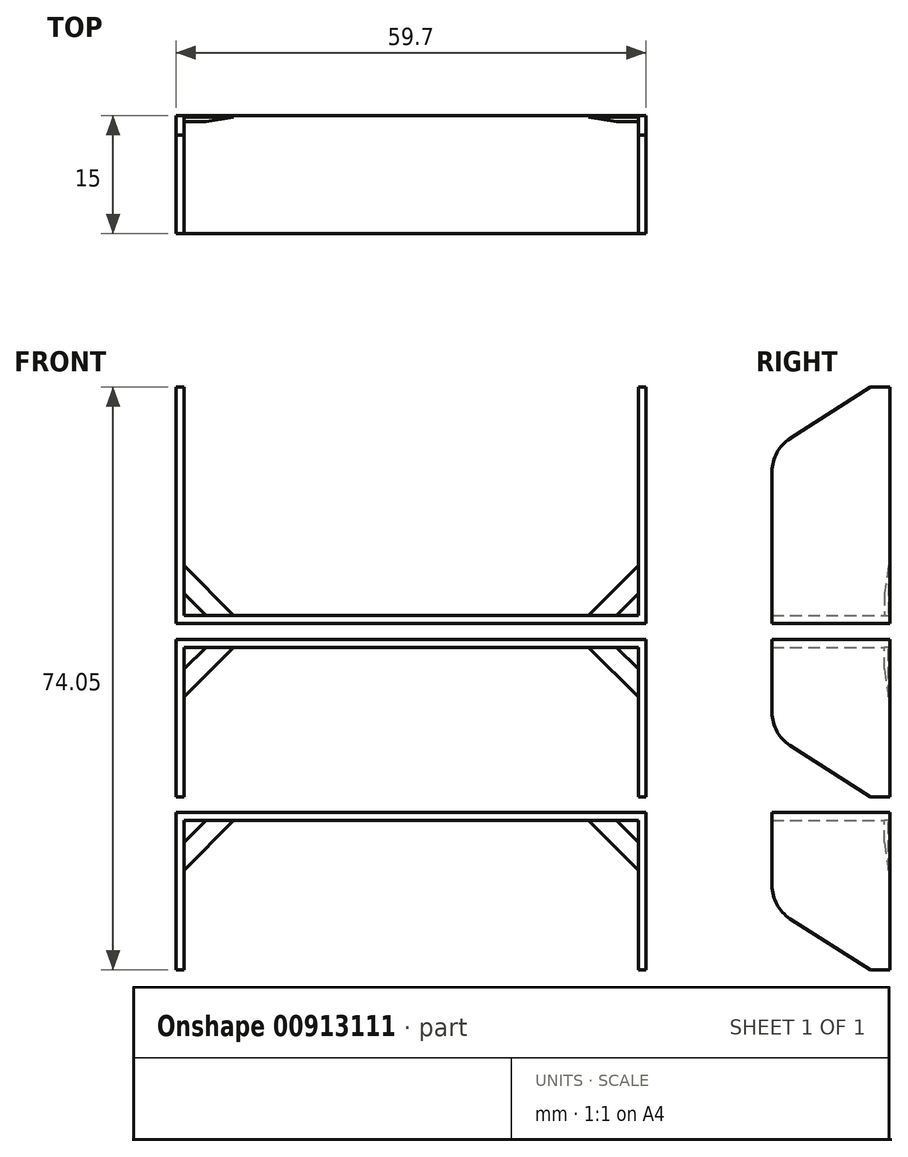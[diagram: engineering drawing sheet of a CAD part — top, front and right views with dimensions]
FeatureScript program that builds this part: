
annotation { "Feature Type Name" : "Feature", "Feature Type Description" : "" }
export const myFeature = defineFeature(function(context is Context, id is Id, definition is map)
    precondition{}
    {
        {
            var Q0;
            Q0=qCreatedBy(makeId("Front.planeOp"),FACE);
            var sketch = newSketch(context, id + "F0", { "sketchPlane" : qUnion([Q0])});
            skLineSegment(sketch, "E0", {"start": v(-40.12, 50.5) * mm, "end": v(-40.12, 20.5) * mm});
            skLineSegment(sketch, "E1", {"start": v(-40.12, 20.5) * mm, "end": v(19.58, 20.5) * mm});
            skLineSegment(sketch, "E2", {"start": v(19.58, 20.5) * mm, "end": v(19.58, 50.5) * mm});
            skLineSegment(sketch, "E3", {"start": v(-40.12, 50.5) * mm, "end": v(-39.12, 50.5) * mm});
            skLineSegment(sketch, "E4", {"start": v(-39.12, 50.5) * mm, "end": v(-39.12, 21.5) * mm});
            skLineSegment(sketch, "E5", {"start": v(-39.12, 21.5) * mm, "end": v(18.58, 21.5) * mm});
            skLineSegment(sketch, "E6", {"start": v(18.58, 21.5) * mm, "end": v(18.58, 50.5) * mm});
            skLineSegment(sketch, "E7", {"start": v(18.58, 50.5) * mm, "end": v(19.58, 50.5) * mm});
            skLineSegment(sketch, "E8", {"start": v(-39.12, 21.5) * mm, "end": v(-39.12, 20.5) * mm, "construction": true});
            skLineSegment(sketch, "E9", {"start": v(-39.12, 27.82) * mm, "end": v(-32.8, 21.5) * mm});
            skLineSegment(sketch, "E10", {"start": v(-10.27, 21.5) * mm, "end": v(-10.27, 32.03) * mm, "construction": true});
            skLineSegment(sketch, "E11.MirrorCS", {"start": v(18.58, 27.82) * mm, "end": v(12.27, 21.5) * mm});
            skSolve(sketch);
        }
        {
            var Q0;
            Q0=qCreatedBy(makeId("Front.planeOp"),FACE);
            var sketch = newSketch(context, id + "F1", { "sketchPlane" : qUnion([Q0])});
            skLineSegment(sketch, "E12", {"start": v(19.58, -1.54) * mm, "end": v(19.58, 18.46) * mm});
            skLineSegment(sketch, "E13", {"start": v(19.58, 18.46) * mm, "end": v(-40.12, 18.46) * mm});
            skLineSegment(sketch, "E14", {"start": v(-40.12, 18.46) * mm, "end": v(-40.12, -1.54) * mm});
            skLineSegment(sketch, "E15", {"start": v(19.58, -1.54) * mm, "end": v(18.58, -1.54) * mm});
            skLineSegment(sketch, "E16", {"start": v(18.58, -1.54) * mm, "end": v(18.58, 17.46) * mm});
            skLineSegment(sketch, "E17", {"start": v(18.58, 17.46) * mm, "end": v(-39.12, 17.46) * mm});
            skLineSegment(sketch, "E18", {"start": v(-39.12, 17.46) * mm, "end": v(-39.12, -1.54) * mm});
            skLineSegment(sketch, "E19", {"start": v(-39.12, -1.54) * mm, "end": v(-40.12, -1.54) * mm});
            skLineSegment(sketch, "E20", {"start": v(18.58, 17.46) * mm, "end": v(18.58, 18.46) * mm, "construction": true});
            skLineSegment(sketch, "E21", {"start": v(19.58, 20.5) * mm, "end": v(19.58, 10.1) * mm, "construction": true});
            skLineSegment(sketch, "E22", {"start": v(-32.8, 17.46) * mm, "end": v(-39.12, 11.14) * mm});
            skLineSegment(sketch, "E23", {"start": v(-10.27, 17.46) * mm, "end": v(-10.27, 10.79) * mm, "construction": true});
            skLineSegment(sketch, "E24.MirrorCS", {"start": v(12.27, 17.46) * mm, "end": v(18.58, 11.14) * mm});
            skSolve(sketch);
        }
        {
            var Q0;
            Q0=makeQuery(id+"F0.imprint","IMPRINT",FACE,{"disambiguationData":[TD([[makeQuery(id+"F0.imprint","IMPRINT",EDGE,{"derivedFrom":sQuery(id+"F0.wireOp",EDGE,"E0")}),1.0]])]});
            var Q1;
            Q1=makeQuery(id+"F1.imprint","IMPRINT",FACE,{"disambiguationData":[TD([[makeQuery(id+"F1.imprint","IMPRINT",EDGE,{"derivedFrom":sQuery(id+"F1.wireOp",EDGE,"E12")}),1.0]])]});
            extrude(context, id + "F2", {"entities" : qUnion([Q0, Q1]), "depth" : 15 * mm, "offsetDistance" : 25 * mm});
        }
        {
            var Q0;
            {var subQ3=sQuery(id+"F0.wireOp",EDGE,"E9");Q0=makeQuery(id+"F0.imprint","IMPRINT",FACE,{"disambiguationData":[TD([[makeQuery(id+"F0.imprint","IMPRINT",EDGE,{"derivedFrom":subQ3}),-1.0]])]});}
            var Q1;
            {var subQ3=sQuery(id+"F0.wireOp",EDGE,"E11.MirrorCS");Q1=makeQuery(id+"F0.imprint","IMPRINT",FACE,{"disambiguationData":[TD([[makeQuery(id+"F0.imprint","IMPRINT",EDGE,{"derivedFrom":subQ3}),1.0]])]});}
            var Q2;
            {var subQ3=sQuery(id+"F1.wireOp",EDGE,"E24.MirrorCS");Q2=makeQuery(id+"F1.imprint","IMPRINT",FACE,{"disambiguationData":[TD([[makeQuery(id+"F1.imprint","IMPRINT",EDGE,{"derivedFrom":subQ3}),1.0]])]});}
            var Q3;
            {var subQ3=sQuery(id+"F1.wireOp",EDGE,"E22");Q3=makeQuery(id+"F1.imprint","IMPRINT",FACE,{"disambiguationData":[TD([[makeQuery(id+"F1.imprint","IMPRINT",EDGE,{"derivedFrom":subQ3}),-1.0]])]});}
            extrude(context, id + "F3", {"entities" : qUnion([Q0, Q1, Q2, Q3]), "operationType" : NewBodyOperationType.ADD, "depth" : 0.75 * mm, "offsetDistance" : 25 * mm});
        }
        {
            var Q0;
            Q0=makeQuery(id+"F3.opExtrude","CAP_EDGE",EDGE,{"disambiguationData":[OSD([sQuery(id+"F0.wireOp",EDGE,"E11.MirrorCS")])],"isStart":false});
            var Q1;
            Q1=makeQuery(id+"F3.opExtrude","CAP_EDGE",EDGE,{"disambiguationData":[OSD([sQuery(id+"F1.wireOp",EDGE,"E24.MirrorCS")])],"isStart":false});
            chamfer(context, id + "F4", {"entities" : qUnion([Q0, Q1]), "chamferType" : ChamferType.TWO_OFFSETS, "width1" : 2.5 * mm, "oppositeDirection" : false, "width2" : 0.55 * mm, "tangentPropagation" : true});
        }
        {
            var Q0;
            Q0=makeQuery(id+"F3.opExtrude","CAP_EDGE",EDGE,{"disambiguationData":[OSD([sQuery(id+"F0.wireOp",EDGE,"E9")])],"isStart":false});
            var Q1;
            Q1=makeQuery(id+"F3.opExtrude","CAP_EDGE",EDGE,{"disambiguationData":[OSD([sQuery(id+"F1.wireOp",EDGE,"E22")])],"isStart":false});
            chamfer(context, id + "F5", {"entities" : qUnion([Q0, Q1]), "chamferType" : ChamferType.TWO_OFFSETS, "width1" : 0.55 * mm, "oppositeDirection" : false, "width2" : 2.5 * mm, "tangentPropagation" : true});
        }
        {
            var Q0;
            Q0=makeQuery(id+"F2.opExtrude","SWEPT_BODY",BODY,{"disambiguationData":[OSD([sQuery(id+"F1.wireOp",EDGE,"E12"),sQuery(id+"F1.wireOp",EDGE,"E13"),sQuery(id+"F1.wireOp",EDGE,"E14"),sQuery(id+"F1.wireOp",EDGE,"E15"),sQuery(id+"F1.wireOp",EDGE,"E16"),sQuery(id+"F1.wireOp",EDGE,"E17"),sQuery(id+"F1.wireOp",EDGE,"E18"),sQuery(id+"F1.wireOp",EDGE,"E19")])]});
            transform(context, id + "F6", {"entities" : qUnion([Q0]), "transformType" : TransformType.TRANSLATION_3D, "dx" : 0 * mm, "dy" : 0 * mm, "dz" : -22 * mm, "makeCopy" : true});
        }
        {
            var Q0;
            Q0=makeQuery(id+"F2.opExtrude","CAP_EDGE",EDGE,{"disambiguationData":[OSD([sQuery(id+"F1.wireOp",EDGE,"E19")])],"isStart":false});
            var Q1;
            Q1=makeQuery(id+"F2.opExtrude","CAP_EDGE",EDGE,{"disambiguationData":[OSD([sQuery(id+"F1.wireOp",EDGE,"E15")])],"isStart":false});
            var Q2;
            Q2=makeQuery(id+"F2.opExtrude","CAP_EDGE",EDGE,{"disambiguationData":[OSD([sQuery(id+"F0.wireOp",EDGE,"E7")])],"isStart":false});
            var Q3;
            Q3=makeQuery(id+"F2.opExtrude","CAP_EDGE",EDGE,{"disambiguationData":[OSD([sQuery(id+"F0.wireOp",EDGE,"E3")])],"isStart":false});
            var Q4;
            Q4=makeQuery(id+"F6.opPattern","COPY",EDGE,{"derivedFrom":makeQuery(id+"F2.opExtrude","CAP_EDGE",EDGE,{"disambiguationData":[OSD([sQuery(id+"F1.wireOp",EDGE,"E15")])],"isStart":false}),"instanceName":"1"});
            var Q5;
            Q5=makeQuery(id+"F6.opPattern","COPY",EDGE,{"derivedFrom":makeQuery(id+"F2.opExtrude","CAP_EDGE",EDGE,{"disambiguationData":[OSD([sQuery(id+"F1.wireOp",EDGE,"E19")])],"isStart":false}),"instanceName":"1"});
            chamfer(context, id + "F7", {"entities" : qUnion([Q0, Q1, Q2, Q3, Q4, Q5]), "chamferType" : ChamferType.TWO_OFFSETS, "width1" : 12.5 * mm, "oppositeDirection" : false, "width2" : 8 * mm, "tangentPropagation" : true});
        }
        {
            var Q0;
            {var subQ0=sQuery(id+"F0.wireOp",EDGE,"E3");Q0=makeQuery(id+"F7.opChamfer","BLEND_EDGE",EDGE,{"blendedFrom":[makeQuery(id+"F2.opExtrude","CAP_EDGE",EDGE,{"disambiguationData":[OSD([subQ0])],"isStart":false}),makeQuery(id+"F2.opExtrude","CAP_FACE",FACE,{"disambiguationData":[OSD([sQuery(id+"F0.wireOp",EDGE,"E0"),sQuery(id+"F0.wireOp",EDGE,"E1"),sQuery(id+"F0.wireOp",EDGE,"E2"),subQ0,sQuery(id+"F0.wireOp",EDGE,"E4"),sQuery(id+"F0.wireOp",EDGE,"E5"),sQuery(id+"F0.wireOp",EDGE,"E6"),sQuery(id+"F0.wireOp",EDGE,"E7")])],"isStart":false})],"blendedInto":[makeQuery(id+"F2.opExtrude","CAP_FACE",FACE,{"disambiguationData":[OSD([sQuery(id+"F0.wireOp",EDGE,"E0"),sQuery(id+"F0.wireOp",EDGE,"E1"),sQuery(id+"F0.wireOp",EDGE,"E2"),subQ0,sQuery(id+"F0.wireOp",EDGE,"E4"),sQuery(id+"F0.wireOp",EDGE,"E5"),sQuery(id+"F0.wireOp",EDGE,"E6"),sQuery(id+"F0.wireOp",EDGE,"E7")])],"isStart":false})]});}
            var Q1;
            {var subQ0=sQuery(id+"F1.wireOp",EDGE,"E19");Q1=makeQuery(id+"F7.opChamfer","BLEND_EDGE",EDGE,{"blendedFrom":[makeQuery(id+"F2.opExtrude","CAP_EDGE",EDGE,{"disambiguationData":[OSD([subQ0])],"isStart":false}),makeQuery(id+"F2.opExtrude","CAP_FACE",FACE,{"disambiguationData":[OSD([sQuery(id+"F1.wireOp",EDGE,"E12"),sQuery(id+"F1.wireOp",EDGE,"E13"),sQuery(id+"F1.wireOp",EDGE,"E14"),sQuery(id+"F1.wireOp",EDGE,"E15"),sQuery(id+"F1.wireOp",EDGE,"E16"),sQuery(id+"F1.wireOp",EDGE,"E17"),sQuery(id+"F1.wireOp",EDGE,"E18"),subQ0])],"isStart":false})],"blendedInto":[makeQuery(id+"F2.opExtrude","CAP_FACE",FACE,{"disambiguationData":[OSD([sQuery(id+"F1.wireOp",EDGE,"E12"),sQuery(id+"F1.wireOp",EDGE,"E13"),sQuery(id+"F1.wireOp",EDGE,"E14"),sQuery(id+"F1.wireOp",EDGE,"E15"),sQuery(id+"F1.wireOp",EDGE,"E16"),sQuery(id+"F1.wireOp",EDGE,"E17"),sQuery(id+"F1.wireOp",EDGE,"E18"),subQ0])],"isStart":false})]});}
            var Q2;
            {var subQ0=sQuery(id+"F1.wireOp",EDGE,"E15");Q2=makeQuery(id+"F7.opChamfer","BLEND_EDGE",EDGE,{"blendedFrom":[makeQuery(id+"F2.opExtrude","CAP_EDGE",EDGE,{"disambiguationData":[OSD([subQ0])],"isStart":false}),makeQuery(id+"F2.opExtrude","CAP_FACE",FACE,{"disambiguationData":[OSD([sQuery(id+"F1.wireOp",EDGE,"E12"),sQuery(id+"F1.wireOp",EDGE,"E13"),sQuery(id+"F1.wireOp",EDGE,"E14"),subQ0,sQuery(id+"F1.wireOp",EDGE,"E16"),sQuery(id+"F1.wireOp",EDGE,"E17"),sQuery(id+"F1.wireOp",EDGE,"E18"),sQuery(id+"F1.wireOp",EDGE,"E19")])],"isStart":false})],"blendedInto":[makeQuery(id+"F2.opExtrude","CAP_FACE",FACE,{"disambiguationData":[OSD([sQuery(id+"F1.wireOp",EDGE,"E12"),sQuery(id+"F1.wireOp",EDGE,"E13"),sQuery(id+"F1.wireOp",EDGE,"E14"),subQ0,sQuery(id+"F1.wireOp",EDGE,"E16"),sQuery(id+"F1.wireOp",EDGE,"E17"),sQuery(id+"F1.wireOp",EDGE,"E18"),sQuery(id+"F1.wireOp",EDGE,"E19")])],"isStart":false})]});}
            var Q3;
            {var subQ0=sQuery(id+"F1.wireOp",EDGE,"E19");Q3=makeQuery(id+"F7.opChamfer","BLEND_EDGE",EDGE,{"blendedFrom":[makeQuery(id+"F2CpAfzxwNx0uNw_2.opPattern","COPY",EDGE,{"derivedFrom":makeQuery(id+"F2.opExtrude","CAP_EDGE",EDGE,{"disambiguationData":[OSD([subQ0])],"isStart":false}),"instanceName":"1"}),makeQuery(id+"F2CpAfzxwNx0uNw_2.opPattern","COPY",FACE,{"derivedFrom":makeQuery(id+"F2.opExtrude","CAP_FACE",FACE,{"disambiguationData":[OSD([sQuery(id+"F1.wireOp",EDGE,"E12"),sQuery(id+"F1.wireOp",EDGE,"E13"),sQuery(id+"F1.wireOp",EDGE,"E14"),sQuery(id+"F1.wireOp",EDGE,"E15"),sQuery(id+"F1.wireOp",EDGE,"E16"),sQuery(id+"F1.wireOp",EDGE,"E17"),sQuery(id+"F1.wireOp",EDGE,"E18"),subQ0])],"isStart":false}),"instanceName":"1"})],"blendedInto":[makeQuery(id+"F2CpAfzxwNx0uNw_2.opPattern","COPY",FACE,{"derivedFrom":makeQuery(id+"F2.opExtrude","CAP_FACE",FACE,{"disambiguationData":[OSD([sQuery(id+"F1.wireOp",EDGE,"E12"),sQuery(id+"F1.wireOp",EDGE,"E13"),sQuery(id+"F1.wireOp",EDGE,"E14"),sQuery(id+"F1.wireOp",EDGE,"E15"),sQuery(id+"F1.wireOp",EDGE,"E16"),sQuery(id+"F1.wireOp",EDGE,"E17"),sQuery(id+"F1.wireOp",EDGE,"E18"),subQ0])],"isStart":false}),"instanceName":"1"})]});}
            var Q4;
            {var subQ0=sQuery(id+"F0.wireOp",EDGE,"E7");Q4=makeQuery(id+"F7.opChamfer","BLEND_EDGE",EDGE,{"blendedFrom":[makeQuery(id+"F2.opExtrude","CAP_EDGE",EDGE,{"disambiguationData":[OSD([subQ0])],"isStart":false}),makeQuery(id+"F2.opExtrude","CAP_FACE",FACE,{"disambiguationData":[OSD([sQuery(id+"F0.wireOp",EDGE,"E0"),sQuery(id+"F0.wireOp",EDGE,"E1"),sQuery(id+"F0.wireOp",EDGE,"E2"),sQuery(id+"F0.wireOp",EDGE,"E3"),sQuery(id+"F0.wireOp",EDGE,"E4"),sQuery(id+"F0.wireOp",EDGE,"E5"),sQuery(id+"F0.wireOp",EDGE,"E6"),subQ0])],"isStart":false})],"blendedInto":[makeQuery(id+"F2.opExtrude","CAP_FACE",FACE,{"disambiguationData":[OSD([sQuery(id+"F0.wireOp",EDGE,"E0"),sQuery(id+"F0.wireOp",EDGE,"E1"),sQuery(id+"F0.wireOp",EDGE,"E2"),sQuery(id+"F0.wireOp",EDGE,"E3"),sQuery(id+"F0.wireOp",EDGE,"E4"),sQuery(id+"F0.wireOp",EDGE,"E5"),sQuery(id+"F0.wireOp",EDGE,"E6"),subQ0])],"isStart":false})]});}
            var Q5;
            {var subQ0=sQuery(id+"F1.wireOp",EDGE,"E15");Q5=makeQuery(id+"F7.opChamfer","BLEND_EDGE",EDGE,{"blendedFrom":[makeQuery(id+"F2CpAfzxwNx0uNw_2.opPattern","COPY",EDGE,{"derivedFrom":makeQuery(id+"F2.opExtrude","CAP_EDGE",EDGE,{"disambiguationData":[OSD([subQ0])],"isStart":false}),"instanceName":"1"}),makeQuery(id+"F2CpAfzxwNx0uNw_2.opPattern","COPY",FACE,{"derivedFrom":makeQuery(id+"F2.opExtrude","CAP_FACE",FACE,{"disambiguationData":[OSD([sQuery(id+"F1.wireOp",EDGE,"E12"),sQuery(id+"F1.wireOp",EDGE,"E13"),sQuery(id+"F1.wireOp",EDGE,"E14"),subQ0,sQuery(id+"F1.wireOp",EDGE,"E16"),sQuery(id+"F1.wireOp",EDGE,"E17"),sQuery(id+"F1.wireOp",EDGE,"E18"),sQuery(id+"F1.wireOp",EDGE,"E19")])],"isStart":false}),"instanceName":"1"})],"blendedInto":[makeQuery(id+"F2CpAfzxwNx0uNw_2.opPattern","COPY",FACE,{"derivedFrom":makeQuery(id+"F2.opExtrude","CAP_FACE",FACE,{"disambiguationData":[OSD([sQuery(id+"F1.wireOp",EDGE,"E12"),sQuery(id+"F1.wireOp",EDGE,"E13"),sQuery(id+"F1.wireOp",EDGE,"E14"),subQ0,sQuery(id+"F1.wireOp",EDGE,"E16"),sQuery(id+"F1.wireOp",EDGE,"E17"),sQuery(id+"F1.wireOp",EDGE,"E18"),sQuery(id+"F1.wireOp",EDGE,"E19")])],"isStart":false}),"instanceName":"1"})]});}
            var Q6;
            {var subQ0=sQuery(id+"F1.wireOp",EDGE,"E19");Q6=makeQuery(id+"F7.opChamfer","BLEND_EDGE",EDGE,{"blendedFrom":[makeQuery(id+"F6.opPattern","COPY",EDGE,{"derivedFrom":makeQuery(id+"F2.opExtrude","CAP_EDGE",EDGE,{"disambiguationData":[OSD([subQ0])],"isStart":false}),"instanceName":"1"}),makeQuery(id+"F6.opPattern","COPY",FACE,{"derivedFrom":makeQuery(id+"F2.opExtrude","CAP_FACE",FACE,{"disambiguationData":[OSD([sQuery(id+"F1.wireOp",EDGE,"E12"),sQuery(id+"F1.wireOp",EDGE,"E13"),sQuery(id+"F1.wireOp",EDGE,"E14"),sQuery(id+"F1.wireOp",EDGE,"E15"),sQuery(id+"F1.wireOp",EDGE,"E16"),sQuery(id+"F1.wireOp",EDGE,"E17"),sQuery(id+"F1.wireOp",EDGE,"E18"),subQ0])],"isStart":false}),"instanceName":"1"})],"blendedInto":[makeQuery(id+"F6.opPattern","COPY",FACE,{"derivedFrom":makeQuery(id+"F2.opExtrude","CAP_FACE",FACE,{"disambiguationData":[OSD([sQuery(id+"F1.wireOp",EDGE,"E12"),sQuery(id+"F1.wireOp",EDGE,"E13"),sQuery(id+"F1.wireOp",EDGE,"E14"),sQuery(id+"F1.wireOp",EDGE,"E15"),sQuery(id+"F1.wireOp",EDGE,"E16"),sQuery(id+"F1.wireOp",EDGE,"E17"),sQuery(id+"F1.wireOp",EDGE,"E18"),subQ0])],"isStart":false}),"instanceName":"1"})]});}
            var Q7;
            {var subQ0=sQuery(id+"F1.wireOp",EDGE,"E15");Q7=makeQuery(id+"F7.opChamfer","BLEND_EDGE",EDGE,{"blendedFrom":[makeQuery(id+"F6.opPattern","COPY",EDGE,{"derivedFrom":makeQuery(id+"F2.opExtrude","CAP_EDGE",EDGE,{"disambiguationData":[OSD([subQ0])],"isStart":false}),"instanceName":"1"}),makeQuery(id+"F6.opPattern","COPY",FACE,{"derivedFrom":makeQuery(id+"F2.opExtrude","CAP_FACE",FACE,{"disambiguationData":[OSD([sQuery(id+"F1.wireOp",EDGE,"E12"),sQuery(id+"F1.wireOp",EDGE,"E13"),sQuery(id+"F1.wireOp",EDGE,"E14"),subQ0,sQuery(id+"F1.wireOp",EDGE,"E16"),sQuery(id+"F1.wireOp",EDGE,"E17"),sQuery(id+"F1.wireOp",EDGE,"E18"),sQuery(id+"F1.wireOp",EDGE,"E19")])],"isStart":false}),"instanceName":"1"})],"blendedInto":[makeQuery(id+"F6.opPattern","COPY",FACE,{"derivedFrom":makeQuery(id+"F2.opExtrude","CAP_FACE",FACE,{"disambiguationData":[OSD([sQuery(id+"F1.wireOp",EDGE,"E12"),sQuery(id+"F1.wireOp",EDGE,"E13"),sQuery(id+"F1.wireOp",EDGE,"E14"),subQ0,sQuery(id+"F1.wireOp",EDGE,"E16"),sQuery(id+"F1.wireOp",EDGE,"E17"),sQuery(id+"F1.wireOp",EDGE,"E18"),sQuery(id+"F1.wireOp",EDGE,"E19")])],"isStart":false}),"instanceName":"1"})]});}
            fillet(context, id + "F8", {"entities" : qUnion([Q0, Q1, Q2, Q3, Q4, Q5, Q6, Q7]), "radius" : 5 * mm, "tangentPropagation" : true, "allowEdgeOverflow" : false});
        }
    });
